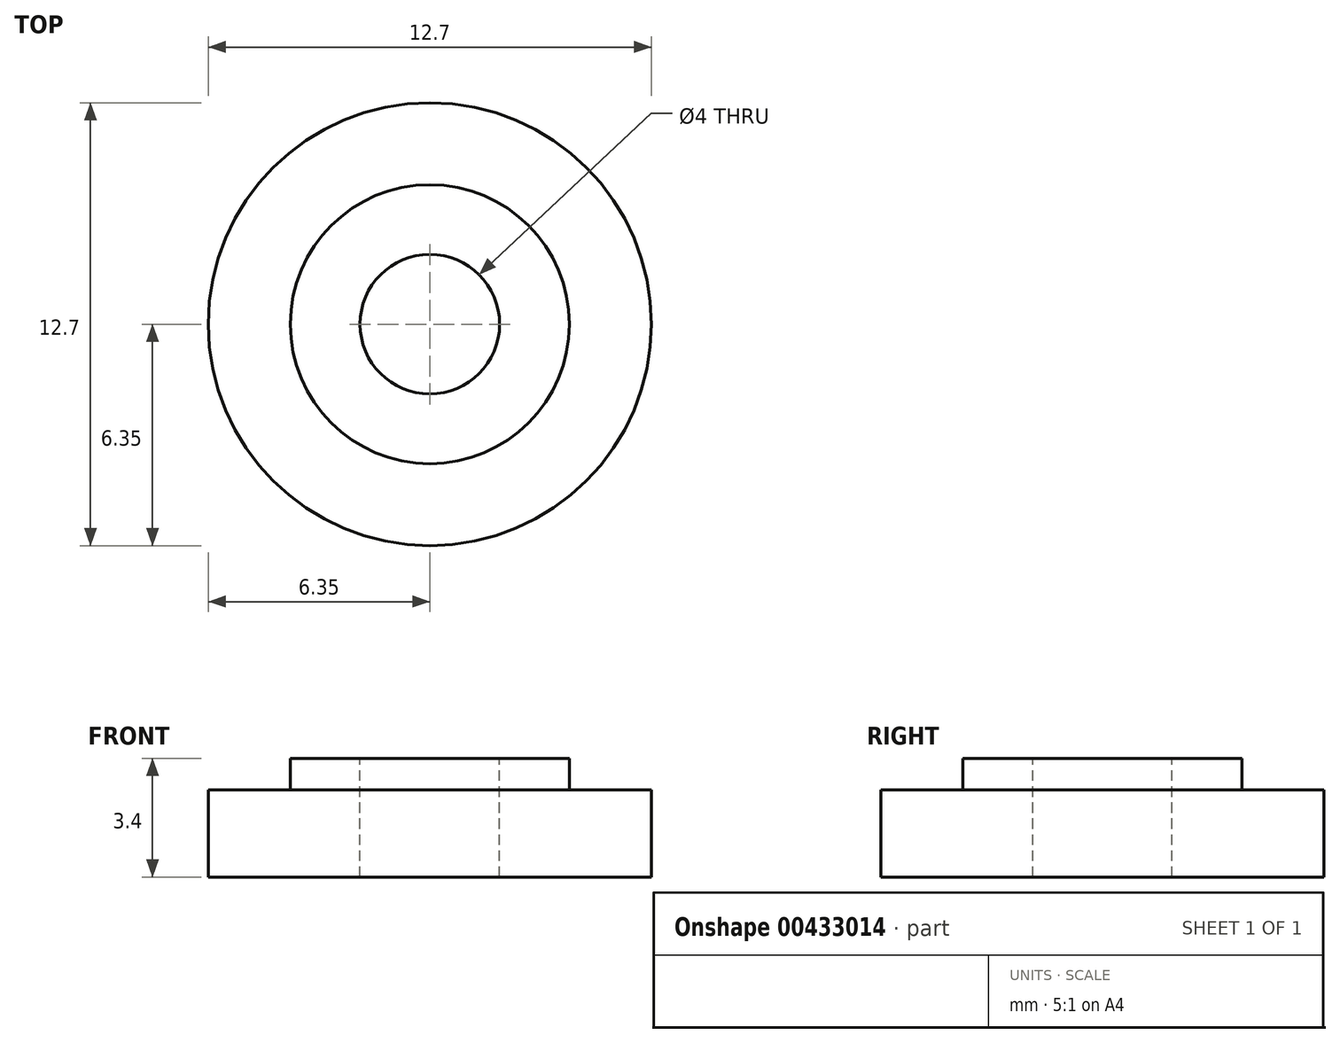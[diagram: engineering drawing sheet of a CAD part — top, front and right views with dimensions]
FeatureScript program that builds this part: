
annotation { "Feature Type Name" : "Feature", "Feature Type Description" : "" }
export const myFeature = defineFeature(function(context is Context, id is Id, definition is map)
    precondition{}
    {
        {
            var Q0;
            Q0=qCreatedBy(makeId("Top.planeOp"),FACE);
            var sketch = newSketch(context, id + "F0", { "sketchPlane" : qUnion([Q0])});
            skCircle(sketch, "E0", {"center": v(0, 0) * mm, "radius": 6.35 * mm});
            skSolve(sketch);
        }
        {
            var Q0;
            Q0=makeQuery(id+"F0.imprint","IMPRINT",FACE,{"disambiguationData":[TD([[makeQuery(id+"F0.imprint","IMPRINT",EDGE,{"derivedFrom":sQuery(id+"F0.wireOp",EDGE,"E0")}),1.0]])]});
            extrude(context, id + "F1", {"entities" : qUnion([Q0]), "depth" : 2.5 * mm, "offsetDistance" : 25 * mm});
        }
        {
            var Q0;
            Q0=makeQuery(id+"F1.opExtrude","CAP_FACE",FACE,{"disambiguationData":[OSD([sQuery(id+"F0.wireOp",EDGE,"E0")])],"isStart":false});
            var sketch = newSketch(context, id + "F2", { "sketchPlane" : qUnion([Q0])});
            skCircle(sketch, "E1", {"center": v(0, 0) * mm, "radius": 4 * mm});
            skSolve(sketch);
        }
        {
            var Q0;
            Q0=makeQuery(id+"F2.imprint","IMPRINT",FACE,{"disambiguationData":[TD([[makeQuery(id+"F2.imprint","IMPRINT",EDGE,{"derivedFrom":sQuery(id+"F2.wireOp",EDGE,"E1")}),1.0]])]});
            extrude(context, id + "F3", {"entities" : qUnion([Q0]), "operationType" : NewBodyOperationType.ADD, "depth" : 0.9 * mm, "offsetDistance" : 25 * mm});
        }
        {
            var Q0;
            Q0=makeQuery(id+"F3.opExtrude","CAP_FACE",FACE,{"disambiguationData":[OSD([sQuery(id+"F2.wireOp",EDGE,"E1")])],"isStart":false});
            var sketch = newSketch(context, id + "F4", { "sketchPlane" : qUnion([Q0])});
            skCircle(sketch, "E2", {"center": v(0, 0) * mm, "radius": 2 * mm});
            skSolve(sketch);
        }
        {
            var Q0;
            Q0=makeQuery(id+"F4.imprint","IMPRINT",FACE,{"disambiguationData":[TD([[makeQuery(id+"F4.imprint","IMPRINT",EDGE,{"derivedFrom":sQuery(id+"F4.wireOp",EDGE,"E2")}),1.0]])]});
            extrude(context, id + "F5", {"entities" : qUnion([Q0]), "operationType" : NewBodyOperationType.REMOVE, "endBound" : BoundingType.THROUGH_ALL, "oppositeDirection" : true, "depth" : 25 * mm, "offsetDistance" : 25 * mm});
        }
    });
